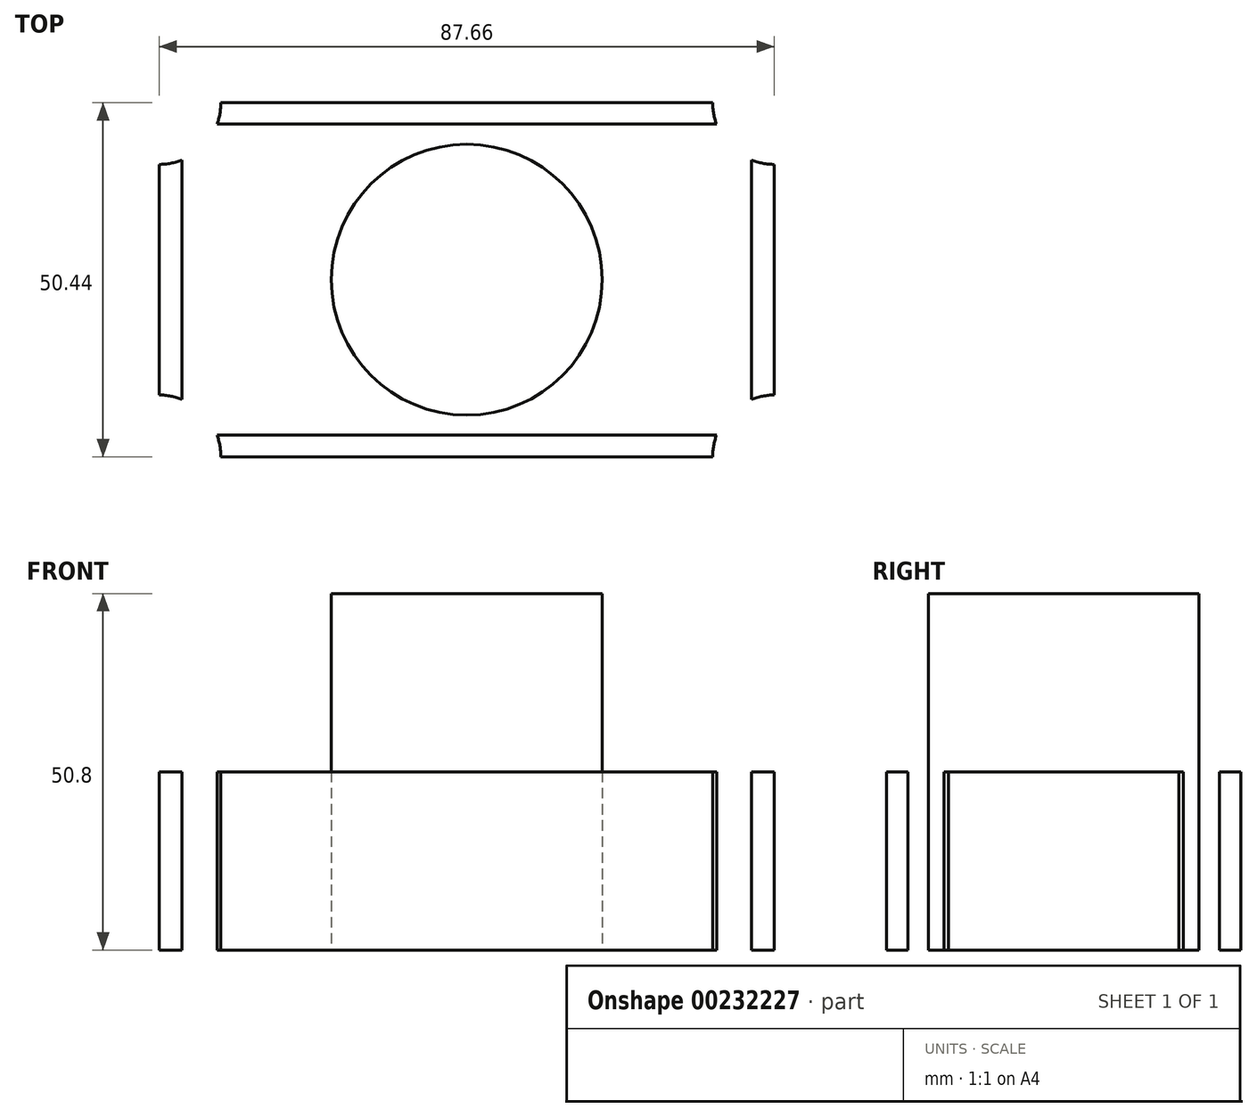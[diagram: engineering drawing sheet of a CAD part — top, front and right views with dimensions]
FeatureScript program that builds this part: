
annotation { "Feature Type Name" : "Feature", "Feature Type Description" : "" }
export const myFeature = defineFeature(function(context is Context, id is Id, definition is map)
    precondition{}
    {
        {
            var Q0;
            Q0=qCreatedBy(makeId("Top.planeOp"),FACE);
            var sketch = newSketch(context, id + "F0", { "sketchPlane" : qUnion([Q0])});
            skLineSegment(sketch, "E0.bottom", {"start": v(35.04, -25.22) * mm, "end": v(-35.04, -25.22) * mm});
            skLineSegment(sketch, "E0.top", {"start": v(35.04, 25.22) * mm, "end": v(-35.04, 25.22) * mm});
            skLineSegment(sketch, "E0.left", {"start": v(43.83, -16.43) * mm, "end": v(43.83, 16.43) * mm});
            skLineSegment(sketch, "E0.right", {"start": v(-43.83, -16.43) * mm, "end": v(-43.83, 16.43) * mm});
            skPoint(sketch, "E0.middle", {"position": v(0, 0) * mm});
            skCircle(sketch, "E1", {"center": v(0, 0) * mm, "radius": 19.3 * mm});
            skCircle(sketch, "E2", {"center": v(-43.83, 25.22) * mm, "radius": 8.8 * mm});
            skCircle(sketch, "E3", {"center": v(43.83, 25.22) * mm, "radius": 8.8 * mm});
            skCircle(sketch, "E4", {"center": v(43.83, -25.22) * mm, "radius": 8.8 * mm});
            skCircle(sketch, "E5", {"center": v(-43.83, -25.22) * mm, "radius": 8.8 * mm});
            skLineSegment(sketch, "E6.bottom", {"start": v(35.59, -22.17) * mm, "end": v(-35.59, -22.17) * mm});
            skLineSegment(sketch, "E6.top", {"start": v(35.59, 22.17) * mm, "end": v(-35.59, 22.17) * mm});
            skLineSegment(sketch, "E6.left", {"start": v(40.57, -17.06) * mm, "end": v(40.57, 17.06) * mm});
            skLineSegment(sketch, "E6.right", {"start": v(-40.57, -17.06) * mm, "end": v(-40.57, 17.06) * mm});
            skPoint(sketch, "E7.orphan", {"position": v(40.57, 22.17) * mm});
            skPoint(sketch, "E8.orphan", {"position": v(40.57, -22.17) * mm});
            skPoint(sketch, "E9.orphan", {"position": v(-40.57, -22.17) * mm});
            skPoint(sketch, "E10.orphan", {"position": v(-40.57, 22.17) * mm});
            skSolve(sketch);
        }
        {
            var Q0;
            {var subQ0=sQuery(id+"F0.wireOp",EDGE,"E0.top");Q0=makeQuery(id+"F0.imprint","IMPRINT",FACE,{"disambiguationData":[TD([[makeQuery(id+"F0.imprint","IMPRINT",EDGE,{"derivedFrom":subQ0}),1.0]])]});}
            var Q1;
            {var subQ0=sQuery(id+"F0.wireOp",EDGE,"E0.left");Q1=makeQuery(id+"F0.imprint","IMPRINT",FACE,{"disambiguationData":[TD([[makeQuery(id+"F0.imprint","IMPRINT",EDGE,{"derivedFrom":subQ0}),1.0]])]});}
            var Q2;
            {var subQ0=sQuery(id+"F0.wireOp",EDGE,"E0.right");Q2=makeQuery(id+"F0.imprint","IMPRINT",FACE,{"disambiguationData":[TD([[makeQuery(id+"F0.imprint","IMPRINT",EDGE,{"derivedFrom":subQ0}),-1.0]])]});}
            var Q3;
            {var subQ0=sQuery(id+"F0.wireOp",EDGE,"E0.bottom");Q3=makeQuery(id+"F0.imprint","IMPRINT",FACE,{"disambiguationData":[TD([[makeQuery(id+"F0.imprint","IMPRINT",EDGE,{"derivedFrom":subQ0}),-1.0]])]});}
            extrude(context, id + "F1", {"entities" : qUnion([Q0, Q1, Q2, Q3]), "depth" : 25.4 * mm});
        }
        {
            var Q0;
            Q0=sQuery(id+"F0.wireOp",EDGE,"E2");
            var Q1;
            Q1=sQuery(id+"F0.wireOp",EDGE,"E5");
            var Q2;
            Q2=sQuery(id+"F0.wireOp",EDGE,"E4");
            var Q3;
            Q3=sQuery(id+"F0.wireOp",EDGE,"E3");
            extrude(context, id + "F2", {"bodyType" : ToolBodyType.SURFACE, "surfaceEntities" : qUnion([Q0, Q1, Q2, Q3]), "depth" : 31.75 * mm});
        }
        {
            var Q0;
            Q0=makeQuery(id+"F0.imprint","IMPRINT",FACE,{"disambiguationData":[TD([[makeQuery(id+"F0.imprint","IMPRINT",EDGE,{"derivedFrom":sQuery(id+"F0.wireOp",EDGE,"E1")}),1.0]])]});
            extrude(context, id + "F3", {"entities" : qUnion([Q0]), "depth" : 50.8 * mm});
        }
    });
